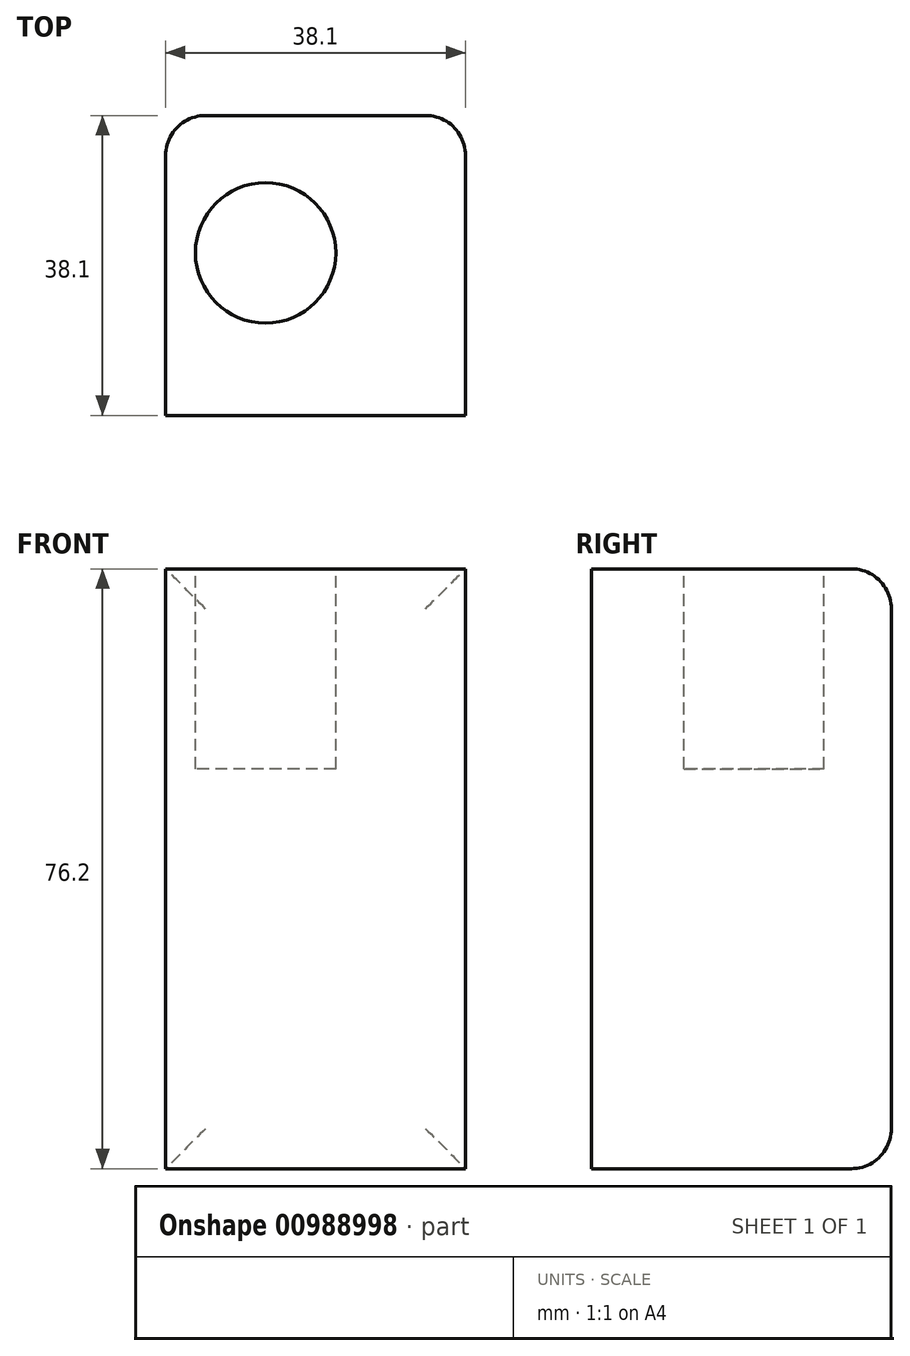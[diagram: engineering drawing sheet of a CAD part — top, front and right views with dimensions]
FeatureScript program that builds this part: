
annotation { "Feature Type Name" : "Feature", "Feature Type Description" : "" }
export const myFeature = defineFeature(function(context is Context, id is Id, definition is map)
    precondition{}
    {
        {
            var Q0;
            Q0=qCreatedBy(makeId("Top.planeOp"),FACE);
            var sketch = newSketch(context, id + "F0", { "sketchPlane" : qUnion([Q0])});
            skLineSegment(sketch, "E0.bottom", {"start": v(-35.07, 4.42) * mm, "end": v(3.03, 4.42) * mm});
            skLineSegment(sketch, "E0.top", {"start": v(-35.07, -33.68) * mm, "end": v(3.03, -33.68) * mm});
            skLineSegment(sketch, "E0.left", {"start": v(-35.07, 4.42) * mm, "end": v(-35.07, -33.68) * mm});
            skLineSegment(sketch, "E0.right", {"start": v(3.03, 4.42) * mm, "end": v(3.03, -33.68) * mm});
            skSolve(sketch);
        }
        {
            var Q0;
            Q0=makeQuery(id+"F0.imprint","IMPRINT",FACE,{"disambiguationData":[TD([[makeQuery(id+"F0.imprint","IMPRINT",EDGE,{"derivedFrom":sQuery(id+"F0.wireOp",EDGE,"E0.bottom")}),-1.0]])]});
            extrude(context, id + "F1", {"entities" : qUnion([Q0]), "depth" : 76.2 * mm, "offsetDistance" : 25.4 * mm});
        }
        {
            var Q0;
            Q0=makeQuery(id+"F1.opExtrude","CAP_FACE",FACE,{"disambiguationData":[OSD([sQuery(id+"F0.wireOp",EDGE,"E0.bottom"),sQuery(id+"F0.wireOp",EDGE,"E0.top"),sQuery(id+"F0.wireOp",EDGE,"E0.left"),sQuery(id+"F0.wireOp",EDGE,"E0.right")])],"isStart":false});
            var sketch = newSketch(context, id + "F2", { "sketchPlane" : qUnion([Q0])});
            skLineSegment(sketch, "E1", {"start": v(-35.07, -13.04) * mm, "end": v(-22.37, -13.04) * mm, "construction": true});
            skCircle(sketch, "E2", {"center": v(-22.37, -13.04) * mm, "radius": 8.92 * mm});
            skSolve(sketch);
        }
        {
            var Q0;
            Q0=makeQuery(id+"F1.opExtrude","CAP_EDGE",EDGE,{"disambiguationData":[OSD([sQuery(id+"F0.wireOp",EDGE,"E0.bottom")])],"isStart":true});
            var Q1;
            Q1=makeQuery(id+"F1.opExtrude","SWEPT_FACE",FACE,{"disambiguationData":[OSD([sQuery(id+"F0.wireOp",EDGE,"E0.bottom")])]});
            fillet(context, id + "F3", {"entities" : qUnion([Q0, Q1]), "radius" : 5.08 * mm, "tangentPropagation" : true, "allowEdgeOverflow" : false});
        }
        {
            var Q0;
            Q0=makeQuery(id+"F2.imprint","IMPRINT",FACE,{"disambiguationData":[TD([[makeQuery(id+"F2.imprint","IMPRINT",EDGE,{"derivedFrom":sQuery(id+"F2.wireOp",EDGE,"E2")}),1.0]])]});
            var Q1;
            Q1=sQuery(id+"F2.wireOp",EDGE,"E2");
            extrude(context, id + "F4", {"entities" : qUnion([Q0]), "operationType" : NewBodyOperationType.REMOVE, "surfaceOperationType" : NewSurfaceOperationType.ADD, "surfaceEntities" : qUnion([Q1]), "oppositeDirection" : true, "depth" : 25.4 * mm, "offsetDistance" : 25.4 * mm});
        }
    });
